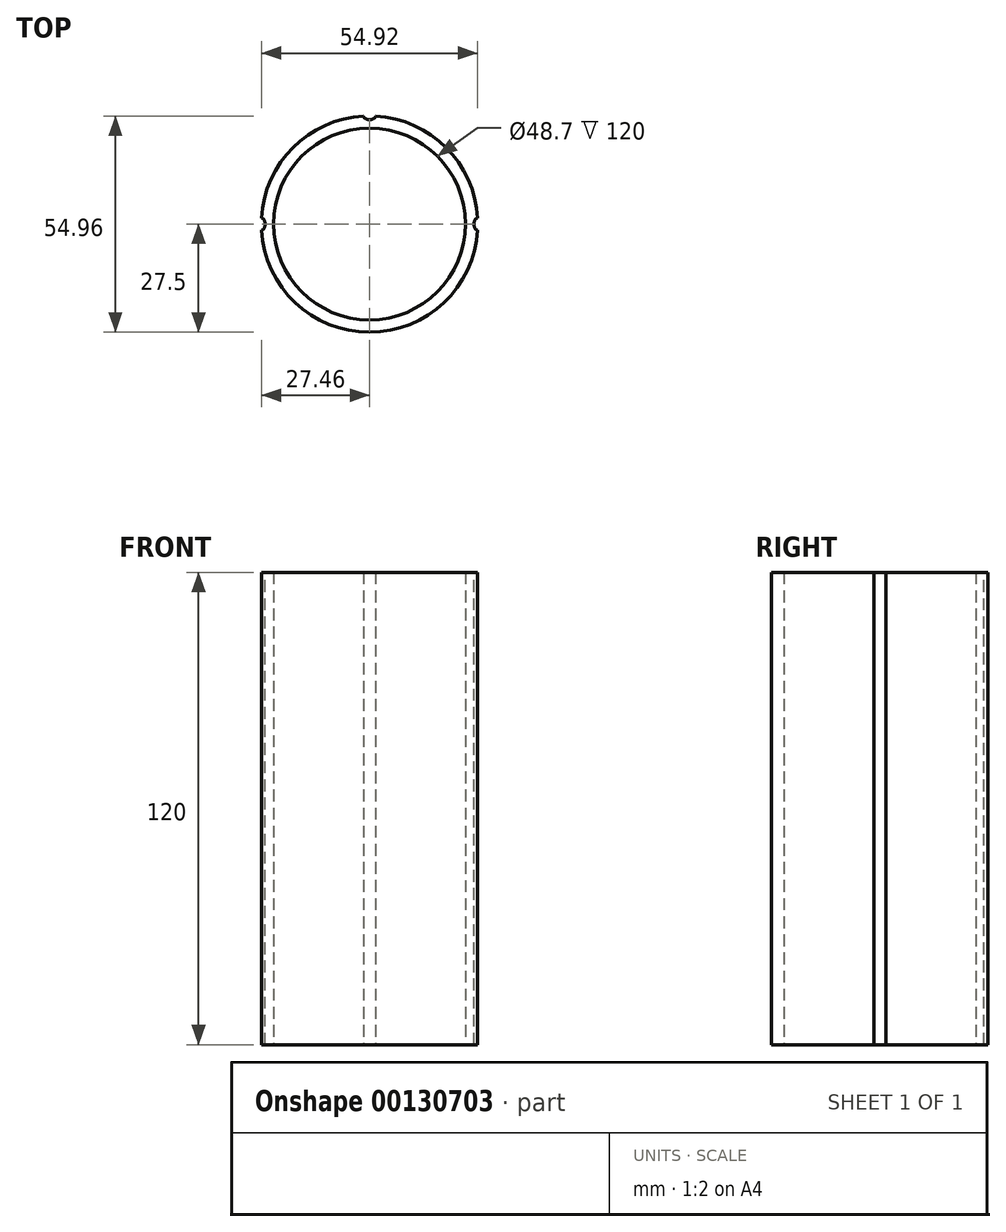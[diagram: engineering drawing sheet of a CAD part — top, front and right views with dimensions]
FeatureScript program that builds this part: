
annotation { "Feature Type Name" : "Feature", "Feature Type Description" : "" }
export const myFeature = defineFeature(function(context is Context, id is Id, definition is map)
    precondition{}
    {
        {
            var Q0;
            Q0=qCreatedBy(makeId("Top.planeOp"),FACE);
            var sketch = newSketch(context, id + "F0", { "sketchPlane" : qUnion([Q0])});
            skCircle(sketch, "E0", {"center": v(0, 0) * mm, "radius": 24.35 * mm});
            skPoint(sketch, "E1.endSnap0", {"position": v(7.4, -36.16) * mm});
            skPoint(sketch, "E2.start.orphan", {"position": v(-0.72, -27.7) * mm});
            skPoint(sketch, "E3.start.orphan", {"position": v(-8.27, -38.88) * mm});
            skPoint(sketch, "E4.end.orphan", {"position": v(7.4, -38.88) * mm});
            skPoint(sketch, "E5.start.orphan", {"position": v(10.16, -36.16) * mm});
            skArc(sketch, "E6", {"start": v(7.84, -26.36) * mm, "mid": v(21.59, -17.04) * mm, "end": v(27.46, -1.5) * mm});
            skPoint(sketch, "E7.middle", {"position": v(0, -27.5) * mm});
            skLineSegment(sketch, "E8.trimOffspring", {"start": v(-7.97, -30.86) * mm, "end": v(-7.96, -30.98) * mm});
            skPoint(sketch, "E7.bottom.end.orphan", {"position": v(-7.88, -19.32) * mm});
            skPoint(sketch, "E9.orphan", {"position": v(7.8, -19.32) * mm});
            skLineSegment(sketch, "E10.left", {"start": v(10.64, -35.68) * mm, "end": v(10.64, -35.68) * mm});
            skLineSegment(sketch, "E10.right", {"start": v(-10.56, -35.68) * mm, "end": v(-10.56, -35.68) * mm});
            skPoint(sketch, "E10.middle", {"position": v(0.04, -35.68) * mm});
            skPoint(sketch, "E10.cornerSnap0", {"position": v(0.04, -35.68) * mm});
            skPoint(sketch, "E11.endSnap0", {"position": v(-7.96, -30.98) * mm});
            skPoint(sketch, "E12.orphan", {"position": v(-10.6, -26.07) * mm});
            skLineSegment(sketch, "E13", {"start": v(-7.97, -30.86) * mm, "end": v(-7.96, -30.85) * mm});
            skPoint(sketch, "E14.orphan", {"position": v(10.64, -31.02) * mm});
            skPoint(sketch, "E15.orphan", {"position": v(-10.58, -30.87) * mm});
            skLineSegment(sketch, "E16", {"start": v(-24.35, 0) * mm, "end": v(-26.5, 0) * mm});
            skPoint(sketch, "E17.orphan", {"position": v(-0.3, -26.27) * mm});
            skEllipticalArc(sketch, "E18", {});
            skEllipticalArc(sketch, "E19", {});
            skEllipticalArc(sketch, "E20", {});
            skArc(sketch, "E21.trimOffspring", {"start": v(-1.5, 27.46) * mm, "mid": v(-19.45, 19.45) * mm, "end": v(-27.46, 1.5) * mm});
            skArc(sketch, "E22.trimOffspring", {"start": v(-27.46, -1.5) * mm, "mid": v(-21.68, -16.92) * mm, "end": v(-8.13, -26.27) * mm});
            skPoint(sketch, "E23.end.orphan", {"position": v(7.86, -31.02) * mm});
            skPoint(sketch, "E24.orphan", {"position": v(-10.57, -33.28) * mm});
            skPoint(sketch, "E7.top.end.orphan", {"position": v(-7.8, -35.68) * mm});
            skPoint(sketch, "E25.end.orphan", {"position": v(10.64, -33.35) * mm});
            skPoint(sketch, "E25.start.orphan", {"position": v(7.88, -35.68) * mm});
            skPoint(sketch, "E26.start.orphan", {"position": v(-13.66, -30.2) * mm});
            skPoint(sketch, "E27.bottom.end.orphan", {"position": v(-13.66, -27.7) * mm});
            skPoint(sketch, "E27.top.end.orphan", {"position": v(-13.66, -32.7) * mm});
            skPoint(sketch, "E28.orphan", {"position": v(-8.13, -27.7) * mm});
            skPoint(sketch, "E29.start.orphan", {"position": v(7.84, -27.7) * mm});
            skLineSegment(sketch, "E30.trimOffspring", {"start": v(7.88, -35.68) * mm, "end": v(7.88, -35.73) * mm});
            skArc(sketch, "E31", {"start": v(-8.13, -26.27) * mm, "mid": v(-0.15, -27.5) * mm, "end": v(7.84, -26.36) * mm});
            skArc(sketch, "E32.trimOffspring", {"start": v(27.46, 1.5) * mm, "mid": v(19.45, 19.45) * mm, "end": v(1.5, 27.46) * mm});
            skLineSegment(sketch, "E33.left", {"start": v(7.83, -27.5) * mm, "end": v(7.83, -27.5) * mm});
            skLineSegment(sketch, "E33.right", {"start": v(-7.83, -27.5) * mm, "end": v(-7.83, -27.5) * mm});
            skLineSegment(sketch, "E34.bottom", {"start": v(7.84, -27.5) * mm, "end": v(7.83, -27.5) * mm});
            skLineSegment(sketch, "E34.top", {"start": v(7.84, -27.5) * mm, "end": v(7.83, -27.5) * mm});
            skLineSegment(sketch, "E34.left", {"start": v(10.6, -27.5) * mm, "end": v(10.6, -27.5) * mm});
            skLineSegment(sketch, "E34.right", {"start": v(-10.6, -27.5) * mm, "end": v(-10.6, -27.5) * mm});
            skLineSegment(sketch, "E35.trimOffspring", {"start": v(7.84, -27.7) * mm, "end": v(7.84, -27.5) * mm});
            skLineSegment(sketch, "E36", {"start": v(-7.83, -30.92) * mm, "end": v(-7.96, -30.93) * mm});
            skPoint(sketch, "E37.orphan", {"position": v(-7.83, -26.36) * mm});
            skPoint(sketch, "E38.start.orphan", {"position": v(7.86, -30.85) * mm});
            const initialGuessF0  = {"E18": [-0.0275, 0, 0, 1, 0.0015, 0.001, 3.182475167168509, 6.2423027936008735], "E19": [0, 0.0275, 1, 0, 0.0015, 0.001, 3.182475167168509, 6.2423027936008735], "E20": [0.0275, 0, 0, 1, 0.0015, 0.001, 0.040882513578712525, 3.1007101400110773]};
            skSetInitialGuess(sketch, initialGuessF0);
            skSolve(sketch);
        }
        {
            var Q0;
            Q0=makeQuery(id+"F0.imprint","IMPRINT",FACE,{"disambiguationData":[TD([[makeQuery(id+"F0.imprint","IMPRINT",EDGE,{"derivedFrom":sQuery(id+"F0.wireOp",EDGE,"E0")}),-1.0]])]});
            extrude(context, id + "F1", {"entities" : qUnion([Q0]), "depth" : 120 * mm});
        }
    });
